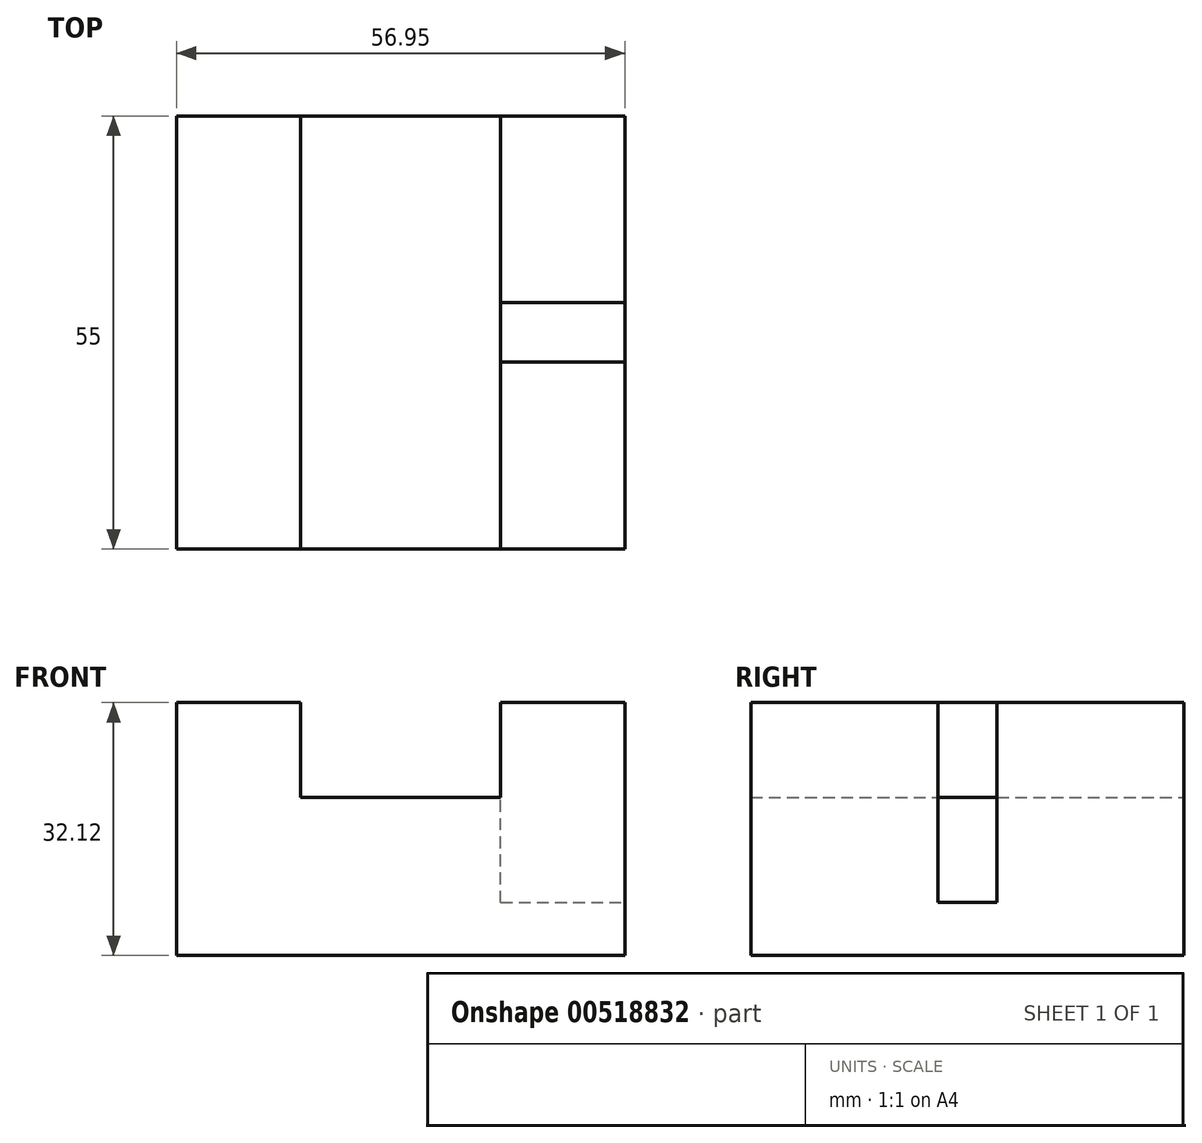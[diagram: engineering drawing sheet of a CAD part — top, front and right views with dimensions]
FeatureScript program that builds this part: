
annotation { "Feature Type Name" : "Feature", "Feature Type Description" : "" }
export const myFeature = defineFeature(function(context is Context, id is Id, definition is map)
    precondition{}
    {
        {
            var Q0;
            Q0=qCreatedBy(makeId("Front.planeOp"),FACE);
            var sketch = newSketch(context, id + "F0", { "sketchPlane" : qUnion([Q0])});
            skLineSegment(sketch, "E0.top", {"start": v(26.75, -27.65) * mm, "end": v(-26.75, -27.65) * mm});
            skLineSegment(sketch, "E0.left", {"start": v(26.75, 27.65) * mm, "end": v(26.75, -27.65) * mm});
            skLineSegment(sketch, "E0.right", {"start": v(-26.75, 27.65) * mm, "end": v(-26.75, -27.65) * mm});
            skPoint(sketch, "E0.middle", {"position": v(0, 0) * mm});
            skCircle(sketch, "E1", {"center": v(0, 27.65) * mm, "radius": 26.75 * mm});
            skCircle(sketch, "E2", {"center": v(0, 27.65) * mm, "radius": 9.42 * mm});
            skSolve(sketch);
        }
        {
            var Q0;
            Q0 = qSketchRegion(id + "F0", true);
            extrude(context, id + "F1", {"entities" : qUnion([Q0]), "depth" : 25.4 * mm});
        }
        {
            var Q0;
            Q0=makeQuery(id+"F1.opExtrude","SWEPT_BODY",BODY,{"disambiguationData":[OSD([sQuery(id+"F0.wireOp",EDGE,"E0.top"),sQuery(id+"F0.wireOp",EDGE,"E0.left"),sQuery(id+"F0.wireOp",EDGE,"E0.right"),sQuery(id+"F0.wireOp",EDGE,"E1"),sQuery(id+"F0.wireOp",EDGE,"E2")])]});
            deleteBodies(context, id + "F2", {"entities" : qUnion([Q0])});
        }
        {
            var Q0;
            Q0=qCreatedBy(makeId("Front.planeOp"),FACE);
            var sketch = newSketch(context, id + "F3", { "sketchPlane" : qUnion([Q0])});
            skLineSegment(sketch, "E3.bottom", {"start": v(0, 0) * mm, "end": v(56.95, 0) * mm});
            skLineSegment(sketch, "E3.top", {"start": v(0, 32.12) * mm, "end": v(15.77, 32.12) * mm});
            skLineSegment(sketch, "E3.left", {"start": v(0, 0) * mm, "end": v(0, 32.12) * mm});
            skLineSegment(sketch, "E3.right", {"start": v(56.95, 0) * mm, "end": v(56.95, 32.12) * mm});
            skLineSegment(sketch, "E4.top", {"start": v(15.77, 20.1) * mm, "end": v(41.19, 20.1) * mm});
            skLineSegment(sketch, "E4.left", {"start": v(15.77, 32.12) * mm, "end": v(15.77, 20.1) * mm});
            skLineSegment(sketch, "E4.right", {"start": v(41.19, 32.12) * mm, "end": v(41.19, 20.1) * mm});
            skLineSegment(sketch, "E5.trimOffspring", {"start": v(41.19, 32.12) * mm, "end": v(56.95, 32.12) * mm});
            skSolve(sketch);
        }
        {
            var Q0;
            Q0 = qSketchRegion(id + "F3", true);
            extrude(context, id + "F4", {"entities" : qUnion([Q0]), "endBound" : BoundingType.SYMMETRIC, "depth" : 55 * mm});
        }
        {
            var Q0;
            Q0=makeQuery(id+"F4.opExtrude","SWEPT_FACE",FACE,{"disambiguationData":[OSD([sQuery(id+"F3.wireOp",EDGE,"E5.trimOffspring")])]});
            var sketch = newSketch(context, id + "F5", { "sketchPlane" : qUnion([Q0])});
            skLineSegment(sketch, "E6.bottom", {"start": v(41.19, -3.72) * mm, "end": v(56.95, -3.72) * mm});
            skLineSegment(sketch, "E6.top", {"start": v(41.19, 3.8) * mm, "end": v(56.95, 3.8) * mm});
            skLineSegment(sketch, "E6.left", {"start": v(41.19, -3.72) * mm, "end": v(41.19, 3.8) * mm});
            skLineSegment(sketch, "E6.right", {"start": v(56.95, -3.72) * mm, "end": v(56.95, 3.8) * mm});
            skSolve(sketch);
        }
        {
            var Q0;
            Q0 = qSketchRegion(id + "F5", true);
            extrude(context, id + "F6", {"entities" : qUnion([Q0]), "operationType" : NewBodyOperationType.REMOVE, "oppositeDirection" : true, "depth" : 25.4 * mm});
        }
    });
